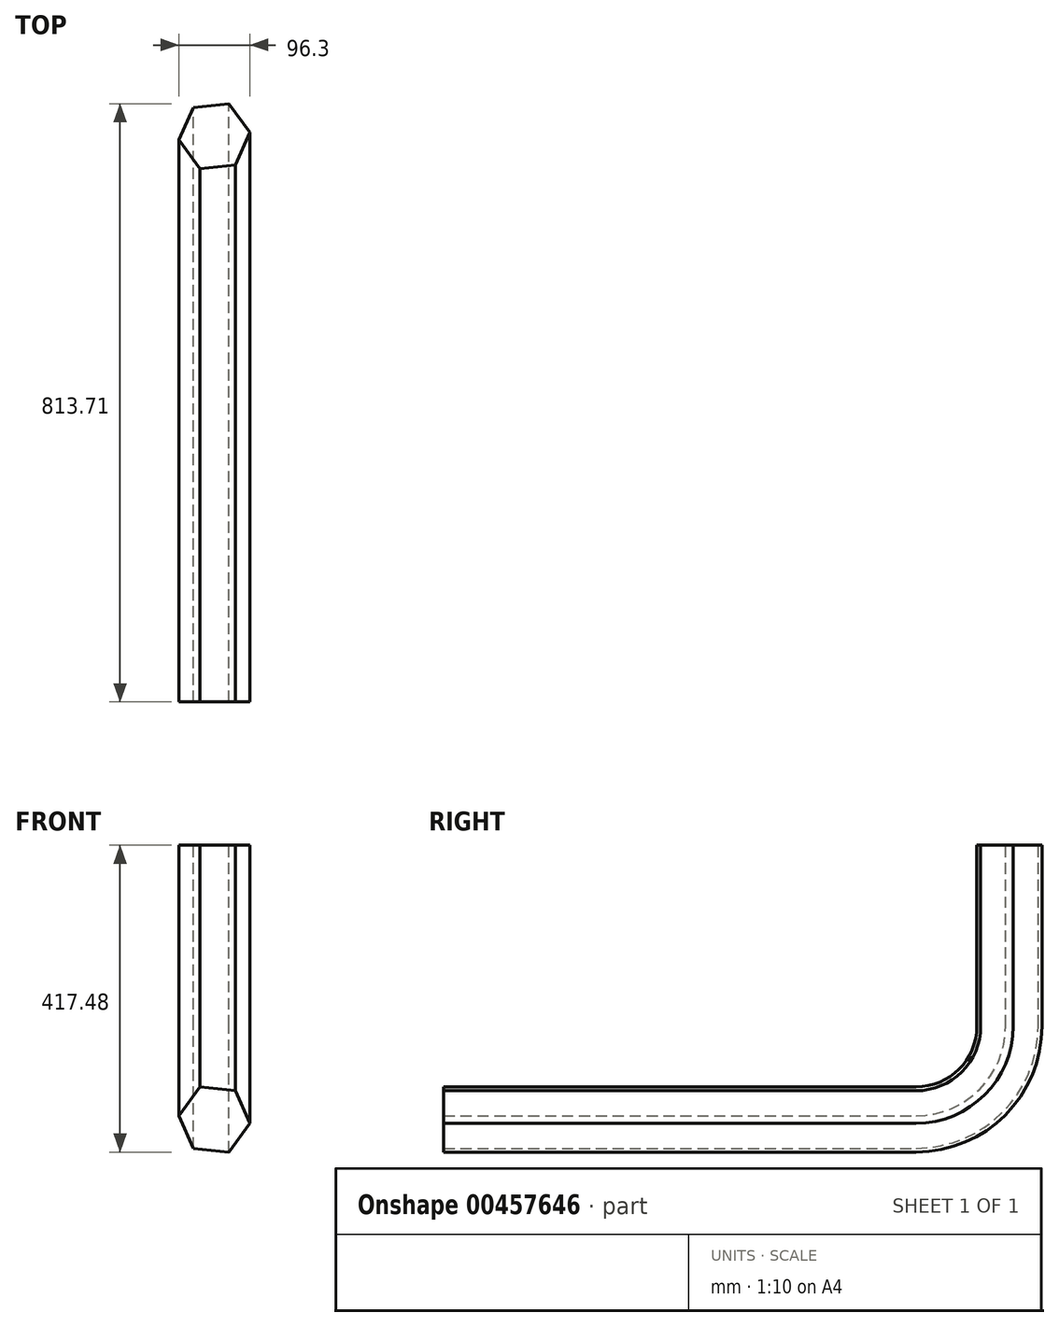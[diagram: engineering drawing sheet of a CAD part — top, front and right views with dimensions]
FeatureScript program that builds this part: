
annotation { "Feature Type Name" : "Feature", "Feature Type Description" : "" }
export const myFeature = defineFeature(function(context is Context, id is Id, definition is map)
    precondition{}
    {
        {
            var Q0;
            Q0=qCreatedBy(makeId("Front.planeOp"),FACE);
            var sketch = newSketch(context, id + "F0", { "sketchPlane" : qUnion([Q0])});
            skCircle(sketch, "E0.cCircle", {"center": v(0, 0) * mm, "radius": 41.94 * mm, "construction": true});
            skLineSegment(sketch, "E0.0", {"start": v(-19.62, 44.28) * mm, "end": v(-48.15, 5.15) * mm});
            skLineSegment(sketch, "E0.1", {"start": v(28.53, 39.13) * mm, "end": v(-19.62, 44.28) * mm});
            skLineSegment(sketch, "E0.2", {"start": v(48.15, -5.15) * mm, "end": v(28.53, 39.13) * mm});
            skLineSegment(sketch, "E0.3", {"start": v(19.62, -44.28) * mm, "end": v(48.15, -5.15) * mm});
            skLineSegment(sketch, "E0.4", {"start": v(-28.53, -39.13) * mm, "end": v(19.62, -44.28) * mm});
            skLineSegment(sketch, "E0.5", {"start": v(-48.15, 5.15) * mm, "end": v(-28.53, -39.13) * mm});
            skPoint(sketch, "E0.0.midPoint", {"position": v(-33.89, 24.71) * mm});
            skSolve(sketch);
        }
        {
            var Q0;
            Q0=qCreatedBy(makeId("Right.planeOp"),FACE);
            var sketch = newSketch(context, id + "F1", { "sketchPlane" : qUnion([Q0])});
            skLineSegment(sketch, "E1", {"start": v(0, 0) * mm, "end": v(642.44, 0) * mm});
            skLineSegment(sketch, "E2", {"start": v(769.44, 127) * mm, "end": v(769.44, 373.2) * mm});
            skPoint(sketch, "E3.visualSharp", {"position": v(769.44, 0) * mm});
            skArc(sketch, "E3.filletArc", {"start": v(642.44, 0) * mm, "mid": v(732.24, 37.2) * mm, "end": v(769.44, 127) * mm});
            skSolve(sketch);
        }
        {
            var Q0;
            Q0 = qSketchRegion(id + "F0", true);
            var Q1;
            Q1=sQuery(id+"F1.wireOp",EDGE,"E1");
            var Q2;
            Q2=sQuery(id+"F1.wireOp",EDGE,"E3.filletArc");
            var Q3;
            Q3=sQuery(id+"F1.wireOp",EDGE,"E2");
            sweep(context, id + "F2", {"profiles" : qUnion([Q0]), "path" : qUnion([Q1, Q2, Q3])});
        }
    });
